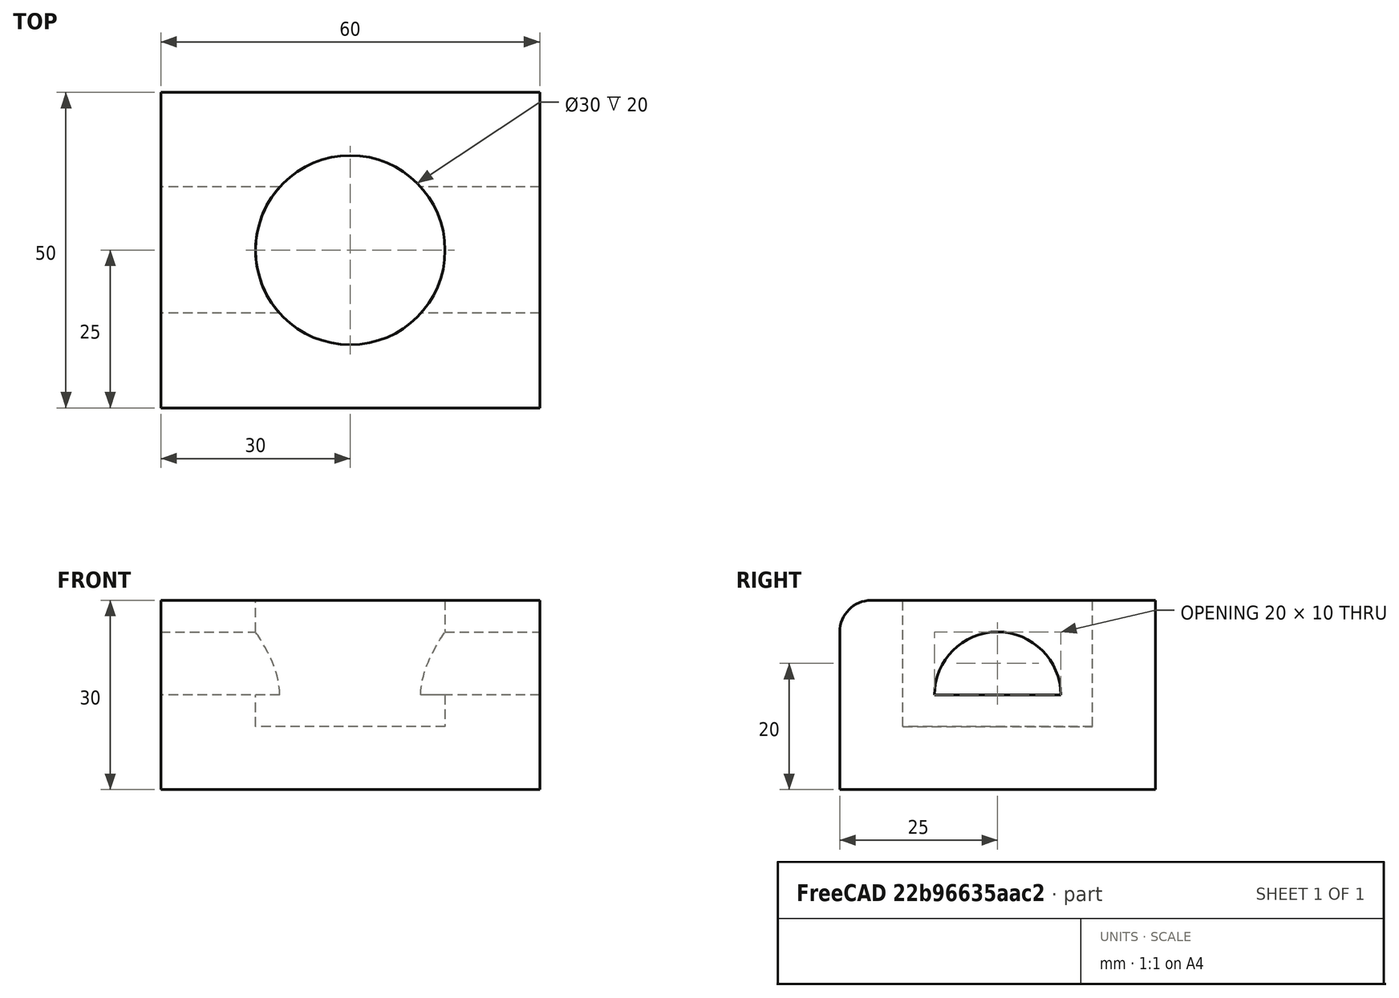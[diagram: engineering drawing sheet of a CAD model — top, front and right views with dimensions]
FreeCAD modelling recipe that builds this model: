
FCSTD DOCUMENT  (FreeCAD 1.0R39109 (Git))
Label: test
License: All rights reserved
LicenseURL: https://en.wikipedia.org/wiki/All_rights_reserved
objects: TechDraw::DrawViewDimension×8, TechDraw::DrawProjGroupItem×5, Sketcher::SketchObject×3, PartDesign::Pocket×2, TechDraw::DrawViewAnnotation×2, PartDesign::Pad×1, PartDesign::Fillet×1, PartDesign::Body×1, TechDraw::DrawSVGTemplate×1, TechDraw::DrawViewBalloon×1, TechDraw::DrawViewSection×1, TechDraw::DrawProjGroup×1, TechDraw::DrawPage×1
note: 33 computed .brp shape members not serialized (recipe doc carries the construction recipe); baked Part::Feature solids carry a one-line shape summary decoded from their .brp

FEATURE [Sketcher::SketchObject] Sketch
  ArcFitTolerance = 1e-06
  AttachmentSupport = -> [XY_Plane]
  FullyConstrained = true
  MakeInternals = false
  MapMode = 5
  sketch-geometry (4):
    g0: LineSegment StartX=-30 StartY=25 StartZ=0 EndX=30 EndY=25 EndZ=0
    g1: LineSegment StartX=30 StartY=25 StartZ=0 EndX=30 EndY=-25 EndZ=0
    g2: LineSegment StartX=30 StartY=-25 StartZ=0 EndX=-30 EndY=-25 EndZ=0
    g3: LineSegment StartX=-30 StartY=-25 StartZ=0 EndX=-30 EndY=25 EndZ=0
  constraints (11):
    c: Coincident(g0,g1)
    c: Coincident(g1,g2)
    c: Coincident(g2,g3)
    c: Coincident(g3,g0)
    c: DistanceY(g1,g0) = 50
    c: DistanceX(g0,g0) = 60
    c: Vertical(g1)
    c: Horizontal(g0)
    c: Equal(g1,g3)
    c: Parallel(g1,g3)
    c: Symmetric(g0,g2,g-1)
FEATURE [PartDesign::Pad] Pad
  Direction = (0,0,1)
  Length = 30
  Length2 = 10
  Profile = -> Sketch
  ReferenceAxis = -> Sketch [N_Axis]
  Refine = true
  Suppressed = false
  Type = 0
FEATURE [Sketcher::SketchObject] Sketch001
  ArcFitTolerance = 1e-06
  AttachmentSupport = -> [Pad]
  FullyConstrained = true
  MakeInternals = false
  MapMode = 5
  Placement = pos=(0,0,30) rot=(0,0,1;0rad)
  sketch-geometry (1):
    g0: Circle CenterX=0 CenterY=0 CenterZ=0 NormalX=0 NormalY=0 NormalZ=1 AngleXU=0 Radius=15
  constraints (2):
    c: Coincident(g0,g-1)
    c: Radius(g0) = 15
FEATURE [PartDesign::Pocket] Pocket
  BaseFeature = -> Pad
  Direction = (0,0,-1)
  Length = 20
  Length2 = 5
  Profile = -> Sketch001
  ReferenceAxis = -> Sketch001 [N_Axis]
  Refine = true
  Suppressed = false
  Type = 0
FEATURE [Sketcher::SketchObject] Sketch002
  ArcFitTolerance = 1e-06
  AttachmentSupport = -> [Pocket]
  ExternalGeometry = -> [Pocket]
  FullyConstrained = true
  MakeInternals = false
  MapMode = 5
  Placement = pos=(30,0,0) rot=(0.57735,0.57735,0.57735;2.0944rad)
  sketch-geometry (4):
    g0: ArcOfCircle CenterX=0 CenterY=15 CenterZ=0 NormalX=0 NormalY=0 NormalZ=1 AngleXU=0 Radius=10 StartAngle=1e-16 EndAngle=3.14159
    g1: LineSegment StartX=-10 StartY=15 StartZ=0 EndX=10 EndY=15 EndZ=0
    g2: LineSegment [constr] StartX=25 StartY=30 StartZ=0 EndX=-25 EndY=-3.6e-15 EndZ=0
    g3: LineSegment [constr] StartX=-25 StartY=30 StartZ=0 EndX=0 EndY=15 EndZ=0
  constraints (10):
    c: Coincident(g1,g0)
    c: Coincident(g1,g0)
    c: Coincident(g2,g-3)
    c: Coincident(g2,g-4)
    c: Coincident(g3,g-4)
    c: Symmetric(g2,g2,g3)
    c: Diameter(g0) = 20
    c: Angle(g0) = 3.14159
    c: Coincident(g0,g3)
    c: Parallel(g1,g-1)
FEATURE [PartDesign::Pocket] Pocket001
  BaseFeature = -> Pocket
  Direction = (-1,0,0)
  Length = 5
  Length2 = 5
  Profile = -> Sketch002
  ReferenceAxis = -> Sketch002 [N_Axis]
  Refine = true
  Suppressed = false
  Type = 1
FEATURE [PartDesign::Fillet] Fillet
  Base = -> Pocket001 [Edge16]
  BaseFeature = -> Pocket001
  Radius = 5
  Refine = true
  SupportTransform = false
  Suppressed = false
  UseAllEdges = false
FEATURE [PartDesign::Body] Body
  AllowCompound = false
  Group = -> [Sketch,Pad,Sketch001,Pocket,Sketch002,Pocket001,Fillet]
  Origin = -> Origin
  Tip = -> Fillet
FEATURE [TechDraw::DrawSVGTemplate] Template  label="テンプレート"
  Height = 210
  Orientation = 1
  Template = <userpath>/AppData/Local/Programs/FreeCAD 1.0/data/Mod/TechDraw/Templates/A4_Landscape_blank.svg
  Width = 297
FEATURE [TechDraw::DrawProjGroupItem] View  label="正面図"
  CoarseView = false
  Direction = (1,-1e-16,0)
  Focus = 100
  HardHidden = true
  IsoCount = 0
  IsoHidden = false
  IsoVisible = false
  LockPosition = false
  Perspective = false
  Rotation = 0
  RotationVector = (1,0,0)
  ScaleType = 2
  ScrubCount = 1
  SeamHidden = false
  SeamVisible = false
  SmoothHidden = false
  SmoothVisible = true
  Source = -> [Body]
  Type = 0
  X = 67.2045
  XDirection = (1e-16,1,0)
  Y = 50.4417
FEATURE [TechDraw::DrawViewDimension] Dimension003  label="寸法003"
  AngleOverride = false
  Arbitrary = false
  ArbitraryTolerances = false
  BoxCorners = (2) [(-50,-30,-1e-07),(50,30,1e-07)]
  EqualTolerance = true
  ExtensionAngle = 0
  FormatSpec = %.2w
  FormatSpecOverTolerance = %+.2w
  FormatSpecUnderTolerance = %+.2w
  Inverted = false
  LineAngle = 0
  LockPosition = false
  MeasureType = 1
  OverTolerance = 0
  References2D = -> [View]
  Rotation = 0
  ScaleType = 0
  TheoreticalExact = false
  Type = 1
  UnderTolerance = 0
  X = 0
  Y = 28.7673
FEATURE [TechDraw::DrawViewDimension] Dimension005  label="寸法005"
  AngleOverride = false
  Arbitrary = false
  ArbitraryTolerances = false
  BoxCorners = (2) [(-50,-30,-1e-07),(50,30,1e-07)]
  EqualTolerance = true
  ExtensionAngle = 0
  FormatSpec = ⌀%.2w
  FormatSpecOverTolerance = %+.2w
  FormatSpecUnderTolerance = %+.2w
  Inverted = false
  LineAngle = 0
  LockPosition = false
  MeasureType = 1
  OverTolerance = 0
  References2D = -> [View]
  Rotation = 0
  ScaleType = 0
  TheoreticalExact = false
  Type = 5
  UnderTolerance = 0
  X = 17.7512
  Y = 28.3729
FEATURE [TechDraw::DrawProjGroupItem] View001  label="平面図"
  CoarseView = false
  Direction = (0,0,1)
  Focus = 100
  HardHidden = true
  IsoCount = 0
  IsoHidden = false
  IsoVisible = false
  LockPosition = false
  Perspective = false
  Rotation = 0
  RotationVector = (1,0,0)
  ScaleType = 2
  ScrubCount = 1
  SeamHidden = false
  SeamVisible = false
  SmoothHidden = false
  SmoothVisible = true
  Source = -> [Body]
  Type = 0
  X = 67.3226
  XDirection = (1e-16,1,0)
  Y = 148.107
FEATURE [TechDraw::DrawViewDimension] Dimension006  label="寸法006"
  AngleOverride = false
  Arbitrary = false
  ArbitraryTolerances = false
  BoxCorners = (2) [(-25,-30,-1e-07),(25,30,1e-07)]
  EqualTolerance = true
  ExtensionAngle = 0
  FormatSpec = %.2w
  FormatSpecOverTolerance = %+.2w
  FormatSpecUnderTolerance = %+.2w
  Inverted = false
  LineAngle = 0
  LockPosition = false
  MeasureType = 1
  OverTolerance = 0
  References2D = -> [View001]
  Rotation = 0
  ScaleType = 0
  TheoreticalExact = false
  Type = 1
  UnderTolerance = 0
  X = 0
  Y = 49.9662
FEATURE [TechDraw::DrawViewDimension] Dimension007  label="寸法007"
  AngleOverride = false
  Arbitrary = false
  ArbitraryTolerances = false
  BoxCorners = (2) [(-25,-30,-1e-07),(25,30,1e-07)]
  EqualTolerance = true
  ExtensionAngle = 0
  FormatSpec = %.2w
  FormatSpecOverTolerance = %+.2w
  FormatSpecUnderTolerance = %+.2w
  Inverted = false
  LineAngle = 0
  LockPosition = false
  MeasureType = 1
  OverTolerance = 0
  References2D = -> [View001]
  Rotation = 0
  ScaleType = 0
  TheoreticalExact = false
  Type = 1
  UnderTolerance = 0
  X = 2.5
  Y = 40.197
FEATURE [TechDraw::DrawViewDimension] Dimension008  label="寸法008"
  AngleOverride = false
  Arbitrary = false
  ArbitraryTolerances = false
  BoxCorners = (2) [(-25,-30,-1e-07),(25,30,1e-07)]
  EqualTolerance = true
  ExtensionAngle = 0
  FormatSpec = %.2w
  FormatSpecOverTolerance = %+.2w
  FormatSpecUnderTolerance = %+.2w
  Inverted = false
  LineAngle = 0
  LockPosition = false
  MeasureType = 1
  OverTolerance = 0
  References2D = -> [View001]
  Rotation = 0
  ScaleType = 0
  TheoreticalExact = false
  Type = 2
  UnderTolerance = 0
  X = -48.3869
  Y = 0
FEATURE [TechDraw::DrawViewBalloon] Balloon  label="吹き出し"
  BubbleShape = 1
  EndType = 0
  EndTypeScale = 1
  KinkLength = 5
  LockPosition = false
  OriginX = -23.5355
  OriginY = 13.5355
  Rotation = 0
  ScaleType = 0
  ShapeScale = 1
  SourceView = -> View
  Text = R5
  TextWrapLen = -1
  X = -43.6438
  Y = 29.2081
FEATURE [TechDraw::DrawProjGroupItem] View002  label="側面図"
  CoarseView = false
  Direction = (-2e-16,1,0)
  Focus = 100
  HardHidden = true
  IsoCount = 0
  IsoHidden = false
  IsoVisible = false
  LockPosition = false
  Perspective = false
  Rotation = 0
  RotationVector = (1,0,0)
  ScaleType = 0
  ScrubCount = 1
  SeamHidden = false
  SeamVisible = false
  SmoothHidden = false
  SmoothVisible = true
  Source = -> [Body]
  Type = 0
  X = 153.968
  XDirection = (-1,-2e-16,0)
  Y = 50.4417
FEATURE [TechDraw::DrawViewDimension] Dimension  label="寸法"
  AngleOverride = false
  Arbitrary = false
  ArbitraryTolerances = false
  BoxCorners = (2) [(-30,-15,-1e-07),(30,15,1e-07)]
  EqualTolerance = true
  ExtensionAngle = 0
  FormatSpec = %.2w
  FormatSpecOverTolerance = %+.2w
  FormatSpecUnderTolerance = %+.2w
  Inverted = false
  LineAngle = 0
  LockPosition = false
  MeasureType = 1
  OverTolerance = 0
  References2D = -> [View002]
  Rotation = 0
  ScaleType = 0
  TheoreticalExact = false
  Type = 2
  UnderTolerance = 0
  X = 42.3185
  Y = 0
FEATURE [TechDraw::DrawViewDimension] Dimension009  label="寸法009"
  AngleOverride = false
  Arbitrary = false
  ArbitraryTolerances = false
  BoxCorners = (2) [(-25,-30,-1e-07),(25,30,1e-07)]
  EqualTolerance = true
  ExtensionAngle = 0
  FormatSpec = R%.2w
  FormatSpecOverTolerance = %+.2w
  FormatSpecUnderTolerance = %+.2w
  Inverted = false
  LineAngle = 0
  LockPosition = false
  MeasureType = 1
  OverTolerance = 0
  References2D = -> [View001]
  Rotation = 0
  ScaleType = 0
  TheoreticalExact = false
  Type = 4
  UnderTolerance = 0
  X = 34.6373
  Y = 18.7092
FEATURE [TechDraw::DrawViewSection] SectionView  label="A-A"
  BaseView = -> View002
  CoarseView = false
  CutSurfaceDisplay = 2
  Direction = (-1,-2e-16,0)
  FileGeomPattern = <userpath>\AppData\Local\Programs\FreeCAD 1.0\data\Mod/TechDraw/PAT/FCPAT.pat
  FileHatchPattern = <userpath>\AppData\Local\Programs\FreeCAD 1.0\data\Mod/TechDraw/Patterns/simple.svg
  Focus = 100
  FuseBeforeCut = false
  HardHidden = true
  HatchOffset = (0,0,0)
  HatchRotation = 0
  HatchScale = 1
  IsoCount = 0
  IsoHidden = false
  IsoVisible = false
  LockPosition = false
  NameGeomPattern = Diamond
  Perspective = false
  Rotation = 90
  ScaleType = 0
  ScrubCount = 1
  SeamHidden = false
  SeamVisible = false
  SectionDirection = 4
  SectionLineStretch = 1
  SectionNormal = (-1,-2e-16,0)
  SectionOrigin = (0,0,15)
  SmoothHidden = false
  SmoothVisible = true
  Source = -> [Body]
  TrimAfterCut = false
  UsePreviousCut = false
  X = 244.334
  XDirection = (0,0,1)
  Y = 50.2743
FEATURE [TechDraw::DrawViewDimension] Dimension010  label="寸法010"
  AngleOverride = false
  Arbitrary = false
  ArbitraryTolerances = false
  BoxCorners = (2) [(-25,-15,-1e-07),(25,15,1e-07)]
  EqualTolerance = true
  ExtensionAngle = 0
  FormatSpec = %.2w
  FormatSpecOverTolerance = %+.2w
  FormatSpecUnderTolerance = %+.2w
  Inverted = false
  LineAngle = 0
  LockPosition = false
  MeasureType = 1
  OverTolerance = 0
  References2D = -> [SectionView]
  Rotation = 0
  ScaleType = 0
  TheoreticalExact = false
  Type = 2
  UnderTolerance = 0
  X = 32.7777
  Y = 5
FEATURE [TechDraw::DrawViewAnnotation] Annotation  label="断面A"
  Font = osifont
  LineSpace = 100
  LockPosition = false
  MaxWidth = -1
  Rotation = 0
  ScaleType = 0
  Text = A
  TextSize = 5
  TextStyle = 0
  X = 140.297
  Y = 76.6502
FEATURE [TechDraw::DrawViewAnnotation] Annotation001  label="断面A-A"
  Font = osifont
  LineSpace = 100
  LockPosition = false
  MaxWidth = -1
  Rotation = 0
  ScaleType = 0
  Text = A-A
  TextSize = 5
  TextStyle = 0
  X = 244.334
  Y = 74.4737
FEATURE [TechDraw::DrawProjGroupItem] View003  label="Front"
  CoarseView = false
  Direction = (1,1e-16,-2e-16)
  Focus = 100
  HardHidden = true
  IsoCount = 0
  IsoHidden = false
  IsoVisible = false
  LockPosition = true
  Perspective = false
  Rotation = 0
  RotationVector = (1,0,0)
  ScaleType = 2
  ScrubCount = 1
  SeamHidden = false
  SeamVisible = false
  SmoothHidden = false
  SmoothVisible = true
  Source = -> [Body]
  Type = 0
  X = 0
  XDirection = (-1e-16,1,0)
  Y = 0
FEATURE [TechDraw::DrawProjGroupItem] ProjItem  label="立法図"
  CoarseView = false
  Direction = (0.57735,0.57735,0.57735)
  Focus = 100
  HardHidden = true
  IsoCount = 0
  IsoHidden = false
  IsoVisible = false
  LockPosition = false
  Perspective = false
  Rotation = 0
  RotationVector = (1,0,0)
  ScaleType = 0
  ScrubCount = 1
  SeamHidden = false
  SeamVisible = false
  SmoothHidden = false
  SmoothVisible = true
  Source = -> [Body]
  Type = 7
  X = -78.8909
  XDirection = (-0.707107,0.707107,2e-16)
  Y = -63.9214
FEATURE [TechDraw::DrawProjGroup] ProjGroup
  Anchor = -> View003
  AutoDistribute = true
  LockPosition = false
  ProjectionType = 0
  Rotation = 0
  ScaleType = 0
  Source = -> [Body]
  Views = -> [View003,ProjItem]
  X = 148.5
  Y = 105
  spacingX = 15
  spacingY = 15
FEATURE [TechDraw::DrawPage] Page  label="用紙"
  KeepUpdated = true
  NextBalloonIndex = 2
  ProjectionType = 0
  Template = -> Template
  Views = -> [View,Dimension003,Dimension005,View001,Dimension006,Dimension007,Dimension008,Balloon,View002,Dimension,Dimension009,SectionView,Dimension010,Annotation,Annotation001,ProjGroup]
